# Revit family: SKSMUKabelrinne SKS-Magic® 85 ungelocht FS_FT_820
name_source: partatom
category: Generic Models
revit_build: Autodesk Revit 2017 (Build: 20190508_0315(x64)
units: mm (PartAtom-declared; Revit-internal decimal feet)

## family parameters
Always vertical = Yes
Can host rebar = No
Cut with Voids When Loaded = No
Part Type = Normal
Room Calculation Point = No
Round Connector Dimension = Use Diameter
Shared = No
Work Plane-Based = No

## types (2) — shared parameters
Cut's number = 2
Height = 85 mm  [stored 0.278871 ft]
Length = 3050 mm  [stored 10.0066 ft]
Length 1 = 3000 mm  [stored 9.84252 ft]
Length 2 = 50 mm  [stored 0.164042 ft]
Manufacturer = OBO BETTERMANN
URL = http://www.obo-bettermann.com
Width = 200 mm  [stored 0.656168 ft]
Width 1 = 100 mm  [stored 0.328084 ft]
Width 2 = 7 mm  [stored 0.0229659 ft]

## per-type parameters (varying)
| type | GTIN | Manufacturer Art.No. | Material |
| SKSMU 820 FS | 4012195833468 | 6059766 | Strip-galvanised |
| SKSMU 820 FT | 4012195833581 | 6059783 | Hot-dip galvanised |

note: column(s) folded — value = type name in every type: Article Type

note: [stored X ft] marks values corroborated as IEEE doubles in the binary element streams (Revit-internal decimal feet)

## geometry (parser evidence)
native form markers: Sweep x2
no freeform markers — native parametric forms only
